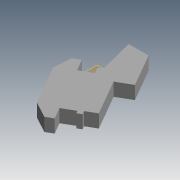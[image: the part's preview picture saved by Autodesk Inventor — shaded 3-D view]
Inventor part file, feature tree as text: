
AUTODESK INVENTOR PART (.ipt)
format: ipt  version: 2014 SP1 (Build 180222100, 222)  size: 196,608 bytes
history: native  units: in
note: dims shown in document units (in); Inventor stores cm internally (conversion verified against a paired STEP export)
features: plane x1, extrude x1, pattern_circular x1, sketch x1
ambient origin geometry x8: Origin, YZ Plane, XZ Plane, XY Plane, X Axis, Y Axis, Z Axis, Center Point
bodies: Solid1 (feature_tree)
feature tree (4):
  plane  "Work Plane3"
  extrude  "Extrusion1"  Depth=0.2835in
  pattern_circular  "Circular Pattern2"  [2 undecoded]
  sketch  "Sketch2"  dims[d1=1.0472in d4=0.2835in d5=0.1028in d6=0.1181in d7=0.0787in d8=0.3409in d9=0.3409in d10=0.1969in d11=0.3409in d12=1.2472in d13=0.1736in d14=0.1148in d17=0.3409in d18=1.15in d20=0.4043in d21=0.1969in d22=0.9126in d23=0.5169in d26=0.3409in d27=0.0in d31=0.5169in d32=1.1811in d33=360.0deg d35=0.1181in]
note: 2 required parameter values undecoded (feature->parameter linkage not recoverable at this tier; creation-order binding heuristic only, values carry confidence <= 0.55)
